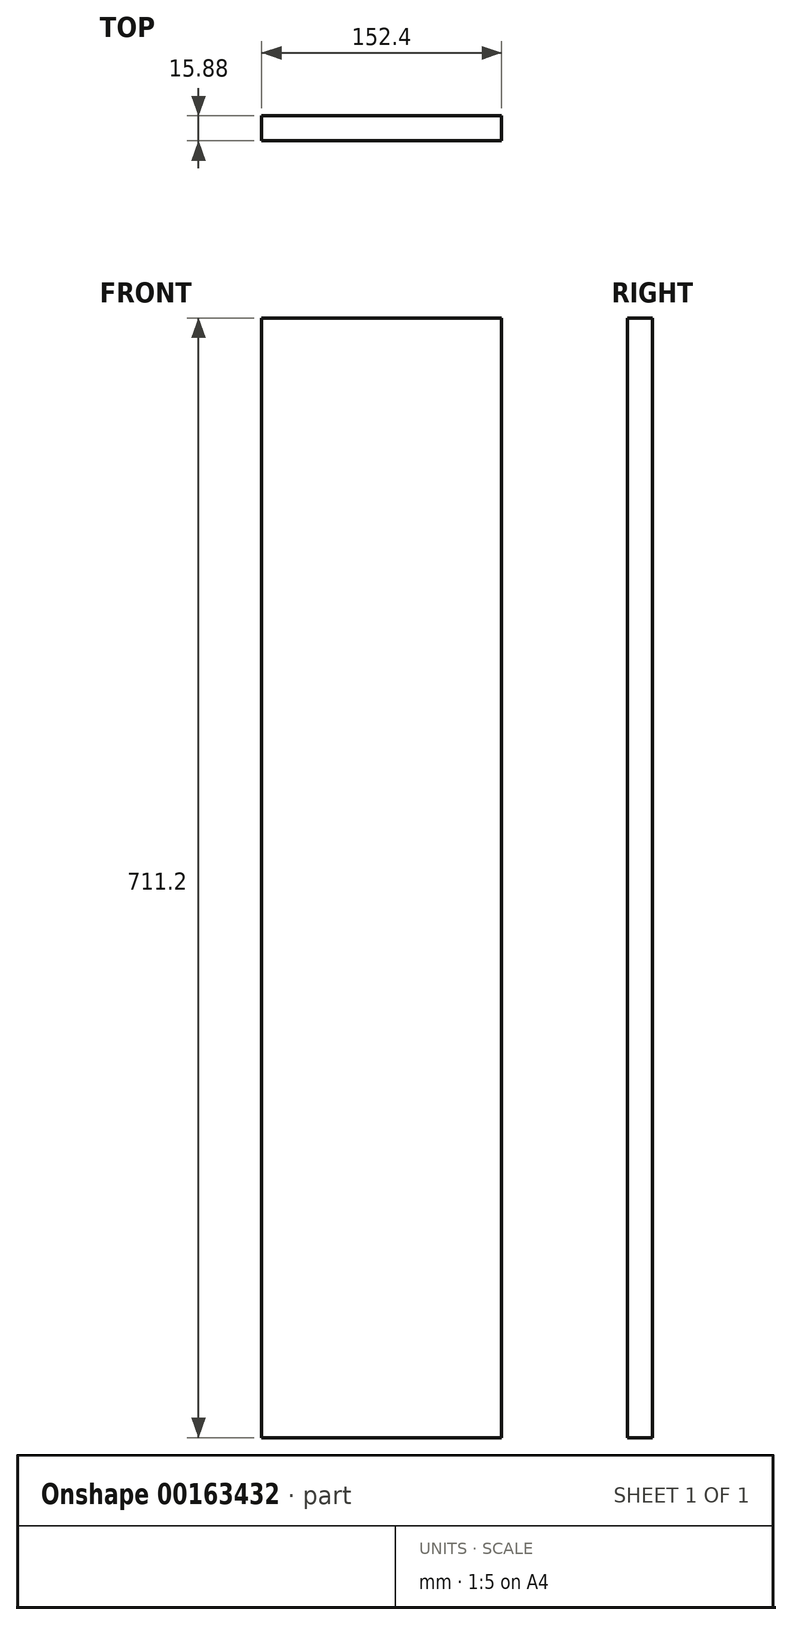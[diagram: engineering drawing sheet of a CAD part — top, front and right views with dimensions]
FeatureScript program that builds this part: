
annotation { "Feature Type Name" : "Feature", "Feature Type Description" : "" }
export const myFeature = defineFeature(function(context is Context, id is Id, definition is map)
    precondition{}
    {
        {
            var Q0;
            Q0=qCreatedBy(makeId("Front.planeOp"),FACE);
            var sketch = newSketch(context, id + "F0", { "sketchPlane" : qUnion([Q0])});
            skLineSegment(sketch, "E0.bottom", {"start": v(0, 0) * mm, "end": v(152.4, 0) * mm});
            skLineSegment(sketch, "E0.top", {"start": v(0, 711.2) * mm, "end": v(152.4, 711.2) * mm});
            skLineSegment(sketch, "E0.left", {"start": v(0, 0) * mm, "end": v(0, 711.2) * mm});
            skLineSegment(sketch, "E0.right", {"start": v(152.4, 0) * mm, "end": v(152.4, 711.2) * mm});
            skSolve(sketch);
        }
        {
            var Q0;
            Q0 = qSketchRegion(id + "F0", true);
            extrude(context, id + "F1", {"entities" : qUnion([Q0]), "depth" : 15.88 * mm});
        }
    });
